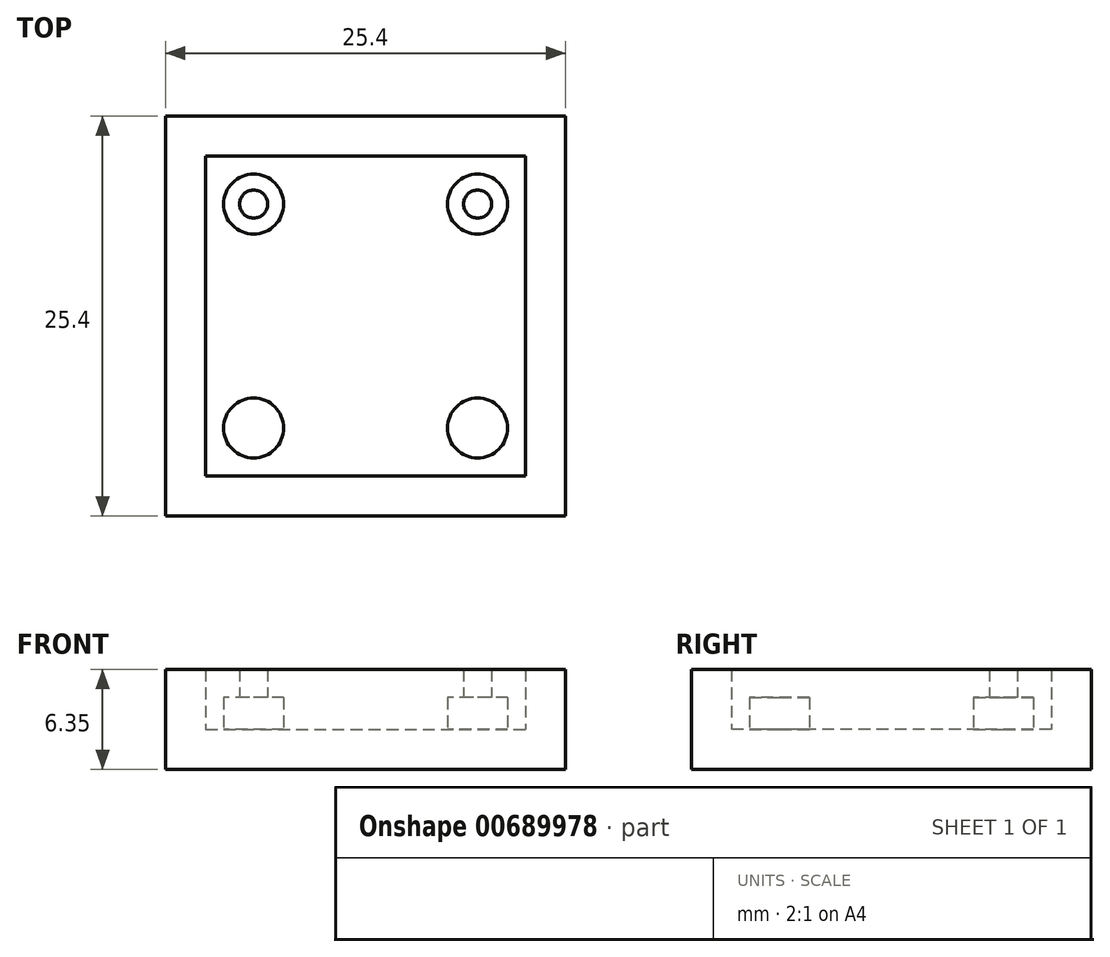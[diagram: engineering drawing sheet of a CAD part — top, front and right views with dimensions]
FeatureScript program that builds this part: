
annotation { "Feature Type Name" : "Feature", "Feature Type Description" : "" }
export const myFeature = defineFeature(function(context is Context, id is Id, definition is map)
    precondition{}
    {
        {
            var Q0;
            Q0=qCreatedBy(makeId("Top.planeOp"),FACE);
            var sketch = newSketch(context, id + "F0", { "sketchPlane" : qUnion([Q0])});
            skLineSegment(sketch, "E0.bottom", {"start": v(-117.09, -7.93) * mm, "end": v(-91.69, -7.93) * mm});
            skLineSegment(sketch, "E0.top", {"start": v(-117.09, -33.33) * mm, "end": v(-91.69, -33.33) * mm});
            skLineSegment(sketch, "E0.left", {"start": v(-117.09, -7.93) * mm, "end": v(-117.09, -33.33) * mm});
            skLineSegment(sketch, "E0.right", {"start": v(-91.69, -7.93) * mm, "end": v(-91.69, -33.33) * mm});
            skSolve(sketch);
        }
        {
            var Q0;
            Q0=makeQuery(id+"F0.imprint","IMPRINT",FACE,{"disambiguationData":[TD([[makeQuery(id+"F0.imprint","IMPRINT",EDGE,{"derivedFrom":sQuery(id+"F0.wireOp",EDGE,"E0.bottom")}),-1.0]])]});
            extrude(context, id + "F1", {"entities" : qUnion([Q0]), "depth" : 6.35 * mm, "offsetDistance" : 25.4 * mm});
        }
        {
            var Q0;
            Q0=makeQuery(id+"F1.opExtrude","CAP_FACE",FACE,{"disambiguationData":[OSD([sQuery(id+"F0.wireOp",EDGE,"E0.bottom"),sQuery(id+"F0.wireOp",EDGE,"E0.top"),sQuery(id+"F0.wireOp",EDGE,"E0.left"),sQuery(id+"F0.wireOp",EDGE,"E0.right")])],"isStart":false});
            shell(context, id + "F2", {"entities" : qUnion([Q0]), "thickness" : 2.54 * mm});
        }
        {
            var Q0;
            Q0=makeQuery(id+"F2.opShell","OFFSET_FACE",FACE,{"disambiguationData":[OSD([sQuery(id+"F0.wireOp",EDGE,"E0.bottom"),sQuery(id+"F0.wireOp",EDGE,"E0.top"),sQuery(id+"F0.wireOp",EDGE,"E0.left"),sQuery(id+"F0.wireOp",EDGE,"E0.right")])]});
            var sketch = newSketch(context, id + "F3", { "sketchPlane" : qUnion([Q0])});
            skCircle(sketch, "E1", {"center": v(-111.5, -13.52) * mm, "radius": 1.9 * mm});
            skLineSegment(sketch, "E2.bottom", {"start": v(-111.5, -13.52) * mm, "end": v(-97.27, -13.52) * mm});
            skLineSegment(sketch, "E2.top", {"start": v(-111.5, -27.75) * mm, "end": v(-97.27, -27.75) * mm});
            skLineSegment(sketch, "E2.left", {"start": v(-111.5, -13.52) * mm, "end": v(-111.5, -27.75) * mm});
            skLineSegment(sketch, "E2.right", {"start": v(-97.27, -13.52) * mm, "end": v(-97.27, -27.75) * mm});
            skCircle(sketch, "E3", {"center": v(-97.27, -13.52) * mm, "radius": 1.9 * mm});
            skCircle(sketch, "E4", {"center": v(-111.5, -27.75) * mm, "radius": 1.9 * mm});
            skCircle(sketch, "E5", {"center": v(-97.27, -27.75) * mm, "radius": 1.9 * mm});
            skSolve(sketch);
        }
        {
            var Q0;
            {var subQ0=sQuery(id+"F3.wireOp",EDGE,"E2.bottom");var subQ1=sQuery(id+"F3.wireOp",EDGE,"E1");var subQ2=makeQuery(id+"F3.imprint","INTERSECT",VERTEX,{"derivedFrom":[subQ1,subQ0]});Q0=makeQuery(id+"F3.imprint","IMPRINT",FACE,{"disambiguationData":[TD([[makeQuery(id+"F3.imprint","IMPRINT",EDGE,{"disambiguationData":[TD([[subQ2,-1.0]])],"derivedFrom":subQ1}),1.0]])]});}
            var Q1;
            {var subQ0=sQuery(id+"F3.wireOp",EDGE,"E2.bottom");var subQ1=sQuery(id+"F3.wireOp",EDGE,"E1");var subQ2=makeQuery(id+"F3.imprint","INTERSECT",VERTEX,{"derivedFrom":[subQ1,subQ0]});Q1=makeQuery(id+"F3.imprint","IMPRINT",FACE,{"disambiguationData":[TD([[makeQuery(id+"F3.imprint","IMPRINT",EDGE,{"disambiguationData":[TD([[subQ2,1.0]])],"derivedFrom":subQ1}),1.0]])]});}
            var Q2;
            {var subQ0=sQuery(id+"F3.wireOp",EDGE,"E2.right");var subQ1=sQuery(id+"F3.wireOp",EDGE,"E2.bottom");var subQ2=makeQuery(id+"F3.imprint","INTERSECT",VERTEX,{"derivedFrom":[subQ1,subQ0]});Q2=makeQuery(id+"F3.imprint","IMPRINT",FACE,{"disambiguationData":[TD([[makeQuery(id+"F3.imprint","IMPRINT",EDGE,{"disambiguationData":[TD([[subQ2,1.0]])],"derivedFrom":subQ1}),1.0]])]});}
            var Q3;
            {var subQ0=sQuery(id+"F3.wireOp",EDGE,"E2.right");var subQ1=sQuery(id+"F3.wireOp",EDGE,"E2.bottom");var subQ2=makeQuery(id+"F3.imprint","INTERSECT",VERTEX,{"derivedFrom":[subQ1,subQ0]});Q3=makeQuery(id+"F3.imprint","IMPRINT",FACE,{"disambiguationData":[TD([[makeQuery(id+"F3.imprint","IMPRINT",EDGE,{"disambiguationData":[TD([[subQ2,1.0]])],"derivedFrom":subQ1}),-1.0]])]});}
            var Q4;
            {var subQ0=sQuery(id+"F3.wireOp",EDGE,"E2.right");var subQ1=sQuery(id+"F3.wireOp",EDGE,"E2.top");var subQ2=makeQuery(id+"F3.imprint","INTERSECT",VERTEX,{"derivedFrom":[subQ1,subQ0]});Q4=makeQuery(id+"F3.imprint","IMPRINT",FACE,{"disambiguationData":[TD([[makeQuery(id+"F3.imprint","IMPRINT",EDGE,{"disambiguationData":[TD([[subQ2,1.0]])],"derivedFrom":subQ1}),1.0]])]});}
            var Q5;
            {var subQ0=sQuery(id+"F3.wireOp",EDGE,"E2.right");var subQ1=sQuery(id+"F3.wireOp",EDGE,"E2.top");var subQ2=makeQuery(id+"F3.imprint","INTERSECT",VERTEX,{"derivedFrom":[subQ1,subQ0]});Q5=makeQuery(id+"F3.imprint","IMPRINT",FACE,{"disambiguationData":[TD([[makeQuery(id+"F3.imprint","IMPRINT",EDGE,{"disambiguationData":[TD([[subQ2,1.0]])],"derivedFrom":subQ1}),-1.0]])]});}
            var Q6;
            {var subQ0=sQuery(id+"F3.wireOp",EDGE,"E2.left");var subQ1=sQuery(id+"F3.wireOp",EDGE,"E2.top");var subQ2=makeQuery(id+"F3.imprint","INTERSECT",VERTEX,{"derivedFrom":[subQ1,subQ0]});Q6=makeQuery(id+"F3.imprint","IMPRINT",FACE,{"disambiguationData":[TD([[makeQuery(id+"F3.imprint","IMPRINT",EDGE,{"disambiguationData":[TD([[subQ2,-1.0]])],"derivedFrom":subQ1}),-1.0]])]});}
            var Q7;
            {var subQ0=sQuery(id+"F3.wireOp",EDGE,"E2.left");var subQ1=sQuery(id+"F3.wireOp",EDGE,"E2.top");var subQ2=makeQuery(id+"F3.imprint","INTERSECT",VERTEX,{"derivedFrom":[subQ1,subQ0]});Q7=makeQuery(id+"F3.imprint","IMPRINT",FACE,{"disambiguationData":[TD([[makeQuery(id+"F3.imprint","IMPRINT",EDGE,{"disambiguationData":[TD([[subQ2,-1.0]])],"derivedFrom":subQ1}),1.0]])]});}
            extrude(context, id + "F4", {"entities" : qUnion([Q0, Q1, Q2, Q3, Q4, Q5, Q6, Q7]), "operationType" : NewBodyOperationType.ADD, "depth" : 2.03 * mm, "offsetDistance" : 25.4 * mm});
        }
        {
            var Q0;
            Q0=makeQuery(id+"F4.opExtrude","CAP_FACE",FACE,{"disambiguationData":[OSD([sQuery(id+"F3.wireOp",EDGE,"E1")])],"isStart":false});
            var sketch = newSketch(context, id + "F5", { "sketchPlane" : qUnion([Q0])});
            skCircle(sketch, "E6", {"center": v(-111.5, -13.52) * mm, "radius": 0.89 * mm});
            skLineSegment(sketch, "E7", {"start": v(-111.5, -13.52) * mm, "end": v(-97.27, -13.52) * mm});
            skCircle(sketch, "E8", {"center": v(-97.27, -13.52) * mm, "radius": 0.89 * mm});
            skSolve(sketch);
        }
        {
            var Q0;
            Q0=makeQuery(id+"F5.imprint","IMPRINT",FACE,{"disambiguationData":[TD([[makeQuery(id+"F5.imprint","IMPRINT",EDGE,{"derivedFrom":sQuery(id+"F5.wireOp",EDGE,"E6")}),1.0]])]});
            var Q1;
            Q1=makeQuery(id+"F5.imprint","IMPRINT",FACE,{"disambiguationData":[TD([[makeQuery(id+"F5.imprint","IMPRINT",EDGE,{"derivedFrom":sQuery(id+"F5.wireOp",EDGE,"E8")}),1.0]])]});
            extrude(context, id + "F6", {"entities" : qUnion([Q0, Q1]), "operationType" : NewBodyOperationType.ADD, "depth" : 1.78 * mm, "offsetDistance" : 25.4 * mm});
        }
    });
